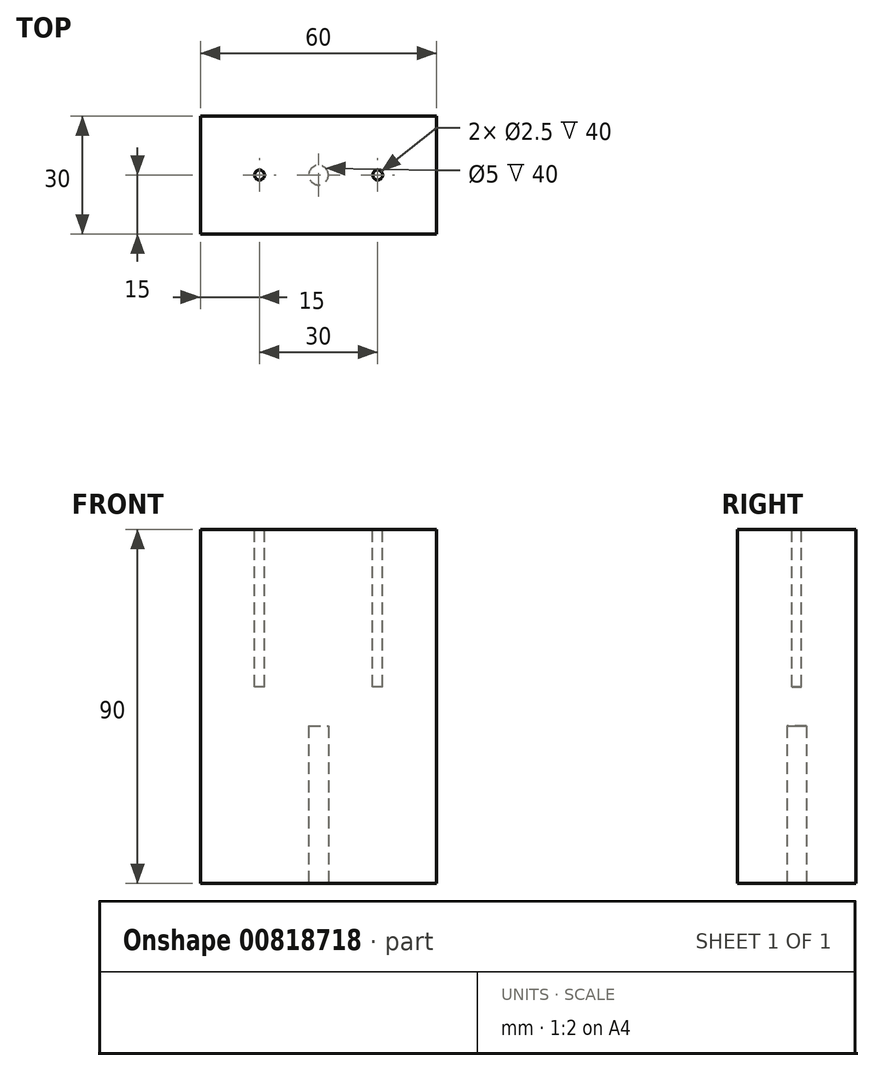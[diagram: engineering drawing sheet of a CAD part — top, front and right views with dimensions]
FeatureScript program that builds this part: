
annotation { "Feature Type Name" : "Feature", "Feature Type Description" : "" }
export const myFeature = defineFeature(function(context is Context, id is Id, definition is map)
    precondition{}
    {
        {
            var Q0;
            Q0=qCreatedBy(makeId("Top.planeOp"),FACE);
            var sketch = newSketch(context, id + "F0", { "sketchPlane" : qUnion([Q0])});
            skLineSegment(sketch, "E0.bottom", {"start": v(-30, 15) * mm, "end": v(30, 15) * mm});
            skLineSegment(sketch, "E0.top", {"start": v(-30, -15) * mm, "end": v(30, -15) * mm});
            skLineSegment(sketch, "E0.left", {"start": v(-30, 15) * mm, "end": v(-30, -15) * mm});
            skLineSegment(sketch, "E0.right", {"start": v(30, 15) * mm, "end": v(30, -15) * mm});
            skPoint(sketch, "E0.middle", {"position": v(0, 0) * mm});
            skSolve(sketch);
        }
        {
            var Q0;
            Q0=makeQuery(id+"F0.imprint","IMPRINT",FACE,{"disambiguationData":[TD([[makeQuery(id+"F0.imprint","IMPRINT",EDGE,{"derivedFrom":sQuery(id+"F0.wireOp",EDGE,"E0.bottom")}),-1.0]])]});
            extrude(context, id + "F1", {"entities" : qUnion([Q0]), "depth" : 90 * mm, "offsetDistance" : 25 * mm});
        }
        {
            var Q0;
            Q0=makeQuery(id+"F1.opExtrude","CAP_FACE",FACE,{"disambiguationData":[OSD([sQuery(id+"F0.wireOp",EDGE,"E0.bottom"),sQuery(id+"F0.wireOp",EDGE,"E0.top"),sQuery(id+"F0.wireOp",EDGE,"E0.left"),sQuery(id+"F0.wireOp",EDGE,"E0.right")])],"isStart":true});
            var sketch = newSketch(context, id + "F2", { "sketchPlane" : qUnion([Q0])});
            skCircle(sketch, "E1", {"center": v(0, 0) * mm, "radius": 2.5 * mm});
            skSolve(sketch);
        }
        {
            var Q0;
            Q0=makeQuery(id+"F2.imprint","IMPRINT",FACE,{"disambiguationData":[TD([[makeQuery(id+"F2.imprint","IMPRINT",EDGE,{"derivedFrom":sQuery(id+"F2.wireOp",EDGE,"E1")}),1.0]])]});
            extrude(context, id + "F3", {"entities" : qUnion([Q0]), "operationType" : NewBodyOperationType.REMOVE, "oppositeDirection" : true, "depth" : 40 * mm, "offsetDistance" : 25 * mm});
        }
        {
            var Q0;
            Q0=makeQuery(id+"F1.opExtrude","CAP_FACE",FACE,{"disambiguationData":[OSD([sQuery(id+"F0.wireOp",EDGE,"E0.bottom"),sQuery(id+"F0.wireOp",EDGE,"E0.top"),sQuery(id+"F0.wireOp",EDGE,"E0.left"),sQuery(id+"F0.wireOp",EDGE,"E0.right")])],"isStart":false});
            var sketch = newSketch(context, id + "F4", { "sketchPlane" : qUnion([Q0])});
            skCircle(sketch, "E2", {"center": v(-15, 0) * mm, "radius": 1.25 * mm});
            skCircle(sketch, "E3", {"center": v(15, 0) * mm, "radius": 1.25 * mm});
            skSolve(sketch);
        }
        {
            var Q0;
            Q0=makeQuery(id+"F4.imprint","IMPRINT",FACE,{"disambiguationData":[TD([[makeQuery(id+"F4.imprint","IMPRINT",EDGE,{"derivedFrom":sQuery(id+"F4.wireOp",EDGE,"E2")}),1.0]])]});
            var Q1;
            Q1=makeQuery(id+"F4.imprint","IMPRINT",FACE,{"disambiguationData":[TD([[makeQuery(id+"F4.imprint","IMPRINT",EDGE,{"derivedFrom":sQuery(id+"F4.wireOp",EDGE,"E3")}),1.0]])]});
            extrude(context, id + "F5", {"entities" : qUnion([Q0, Q1]), "operationType" : NewBodyOperationType.REMOVE, "oppositeDirection" : true, "depth" : 40 * mm, "offsetDistance" : 25 * mm});
        }
    });
